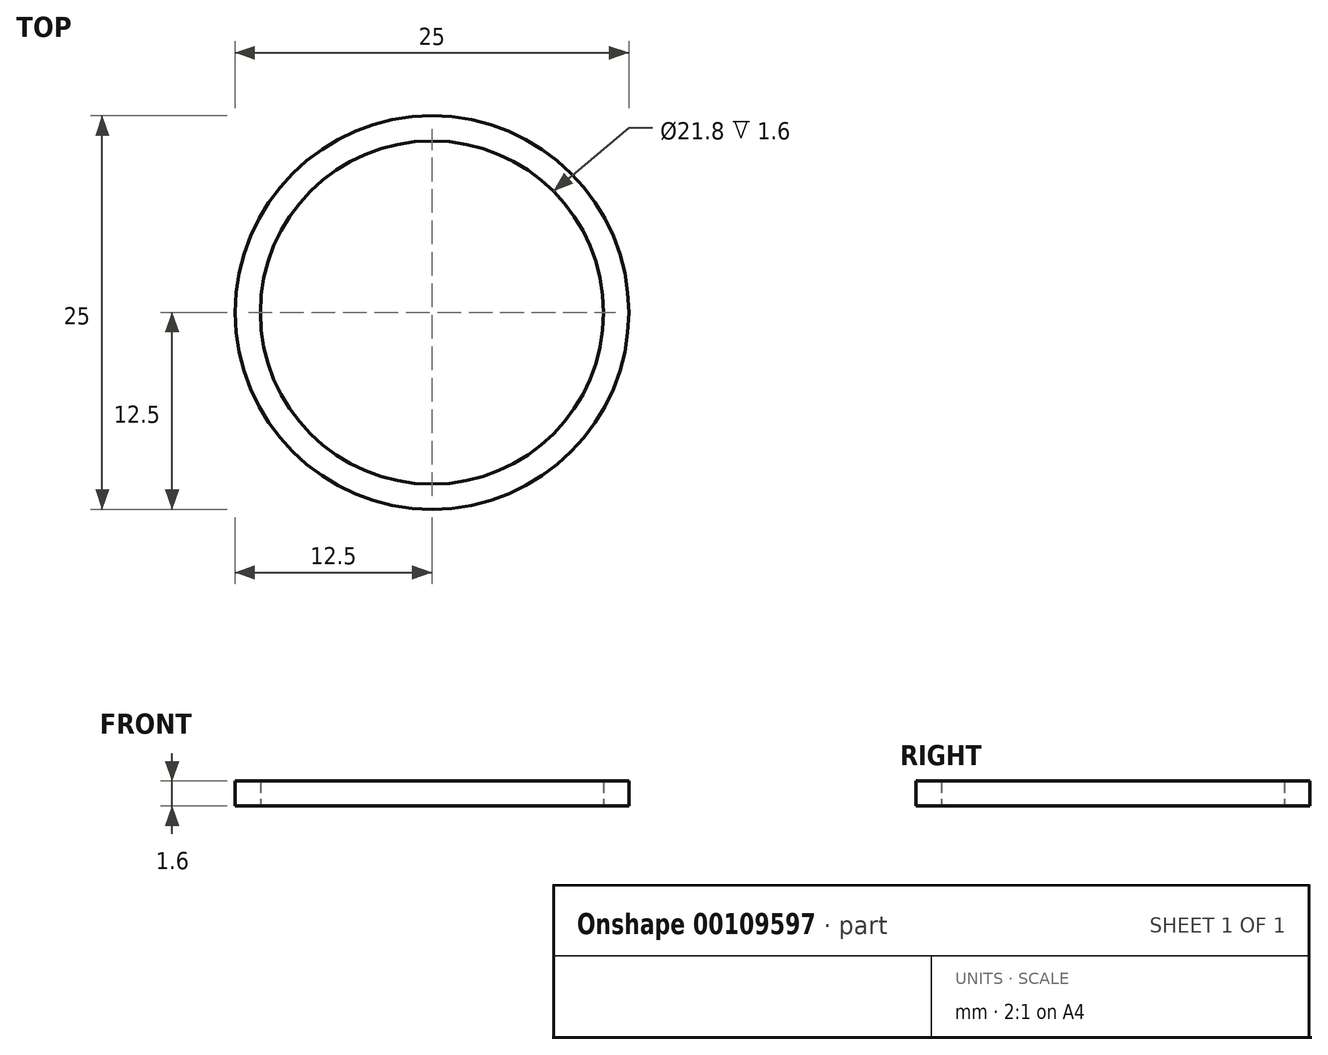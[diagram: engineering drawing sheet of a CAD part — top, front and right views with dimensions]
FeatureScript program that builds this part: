
annotation { "Feature Type Name" : "Feature", "Feature Type Description" : "" }
export const myFeature = defineFeature(function(context is Context, id is Id, definition is map)
    precondition{}
    {
        {
            var Q0;
            Q0=qCreatedBy(makeId("Top.planeOp"),FACE);
            var sketch = newSketch(context, id + "F0", { "sketchPlane" : qUnion([Q0])});
            skCircle(sketch, "E0", {"center": v(0, 0) * mm, "radius": 12.5 * mm});
            skCircle(sketch, "E1.0", {"center": v(0, 0) * mm, "radius": 10.9 * mm});
            skSolve(sketch);
        }
        {
            var Q0;
            Q0=makeQuery(id+"F0.imprint","IMPRINT",FACE,{"disambiguationData":[TD([[makeQuery(id+"F0.imprint","IMPRINT",EDGE,{"derivedFrom":sQuery(id+"F0.wireOp",EDGE,"E0")}),1.0]])]});
            extrude(context, id + "F1", {"entities" : qUnion([Q0]), "depth" : 1.6 * mm});
        }
    });
